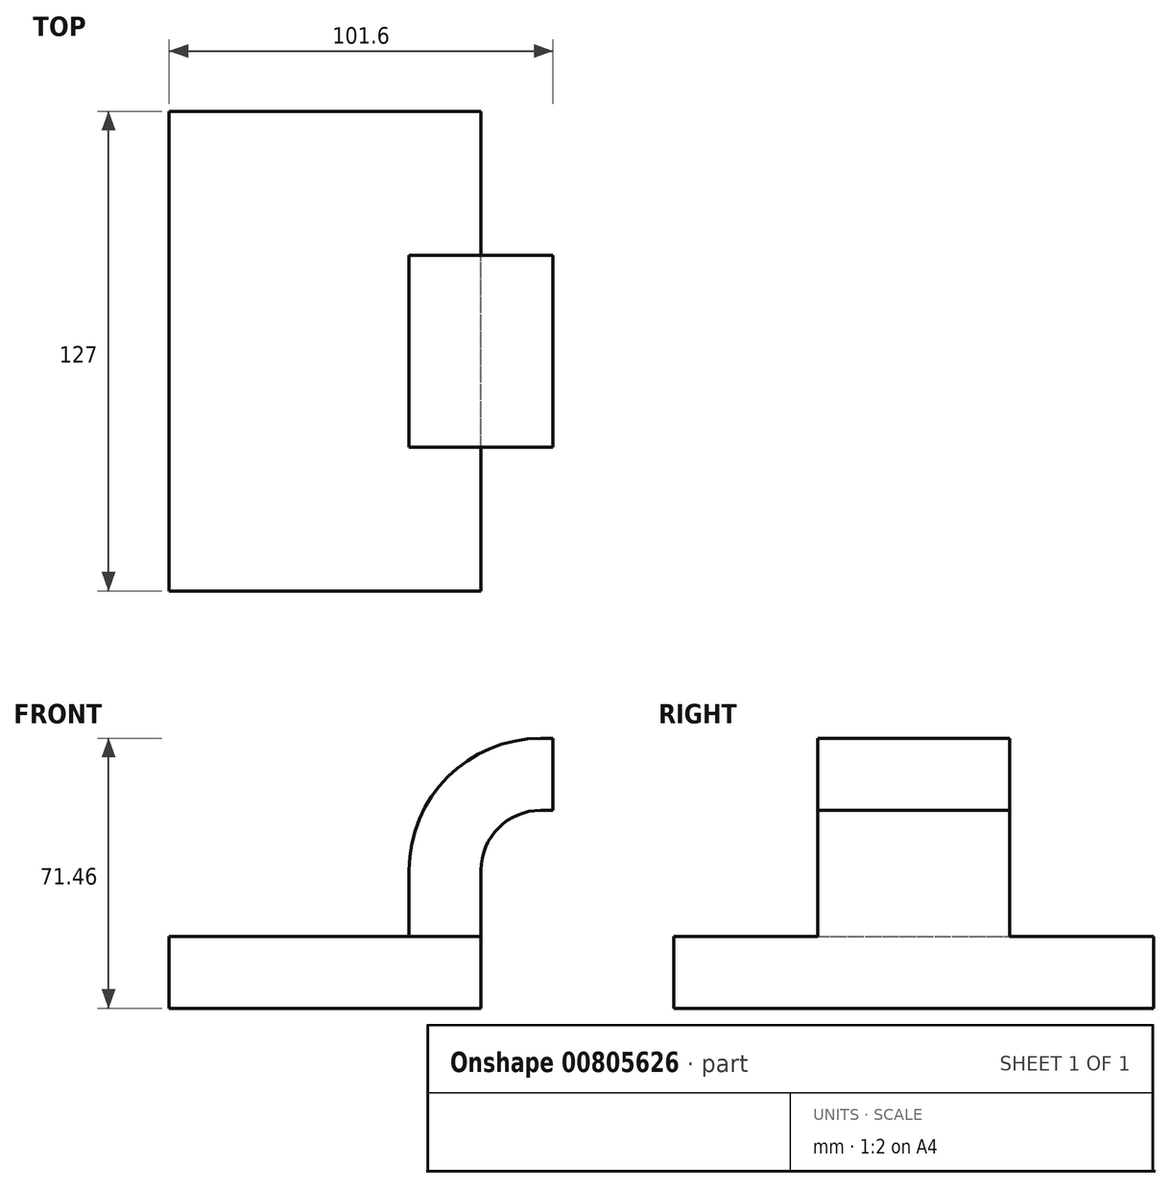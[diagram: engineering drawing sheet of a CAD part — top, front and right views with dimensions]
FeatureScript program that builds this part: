
annotation { "Feature Type Name" : "Feature", "Feature Type Description" : "" }
export const myFeature = defineFeature(function(context is Context, id is Id, definition is map)
    precondition{}
    {
        {
            var Q0;
            Q0=qCreatedBy(makeId("Front.planeOp"),FACE);
            var sketch = newSketch(context, id + "F0", { "sketchPlane" : qUnion([Q0])});
            skLineSegment(sketch, "E0.bottom", {"start": v(41.28, -9.52) * mm, "end": v(-41.28, -9.53) * mm});
            skLineSegment(sketch, "E0.top", {"start": v(41.28, 9.53) * mm, "end": v(-41.28, 9.53) * mm});
            skLineSegment(sketch, "E0.left", {"start": v(41.28, -9.52) * mm, "end": v(41.28, 9.53) * mm});
            skLineSegment(sketch, "E0.right", {"start": v(-41.28, -9.52) * mm, "end": v(-41.28, 9.53) * mm});
            skPoint(sketch, "E0.middle", {"position": v(0, 0) * mm});
            skLineSegment(sketch, "E1.bottom", {"start": v(111.12, 38.1) * mm, "end": v(60.32, 38.1) * mm});
            skLineSegment(sketch, "E1.top", {"start": v(111.12, 66.68) * mm, "end": v(60.32, 66.68) * mm});
            skLineSegment(sketch, "E1.left", {"start": v(111.12, 38.1) * mm, "end": v(111.12, 66.68) * mm});
            skLineSegment(sketch, "E1.right", {"start": v(60.32, 38.1) * mm, "end": v(60.32, 66.68) * mm});
            skPoint(sketch, "E1.middle", {"position": v(85.72, 52.39) * mm});
            skLineSegment(sketch, "E2", {"start": v(41.28, 9.53) * mm, "end": v(41.28, 27) * mm});
            skArc(sketch, "E3", {"start": v(41.27, 27) * mm, "mid": v(45.92, 38.23) * mm, "end": v(57.15, 42.88) * mm});
            skLineSegment(sketch, "E4", {"start": v(57.15, 42.88) * mm, "end": v(82.2, 42.88) * mm});
            skLineSegment(sketch, "E5.0", {"start": v(57.15, 61.93) * mm, "end": v(82.2, 61.93) * mm});
            skArc(sketch, "E5.1", {"start": v(22.23, 27) * mm, "mid": v(32.45, 51.7) * mm, "end": v(57.15, 61.93) * mm});
            skLineSegment(sketch, "E5.2", {"start": v(22.23, 9.53) * mm, "end": v(22.23, 27) * mm});
            skFitSpline(sketch, "E6", {"points": [v(-41.28, 9.53) * mm, v(57.15, 61.93) * mm], "startDerivative": vector(-8.15, 65.35) * mm, "endDerivative": vector(140.73, -14.85) * mm});
            skSolve(sketch);
        }
        {
            var Q0;
            Q0=makeQuery(id+"F0.imprint","IMPRINT",FACE,{"disambiguationData":[TD([[makeQuery(id+"F0.imprint","IMPRINT",EDGE,{"derivedFrom":sQuery(id+"F0.wireOp",EDGE,"E0.bottom")}),-1.0]])]});
            extrude(context, id + "F1", {"entities" : qUnion([Q0]), "endBound" : BoundingType.SYMMETRIC, "depth" : 127 * mm, "offsetDistance" : 25.4 * mm});
        }
        {
            var Q0;
            {var subQ1=sQuery(id+"F0.wireOp",EDGE,"E2");Q0=makeQuery(id+"F0.imprint","IMPRINT",FACE,{"disambiguationData":[TD([[makeQuery(id+"F0.imprint","IMPRINT",EDGE,{"derivedFrom":subQ1}),1.0]])]});}
            extrude(context, id + "F2", {"entities" : qUnion([Q0]), "operationType" : NewBodyOperationType.ADD, "endBound" : BoundingType.SYMMETRIC, "depth" : 50.8 * mm, "offsetDistance" : 25.4 * mm});
        }
    });
